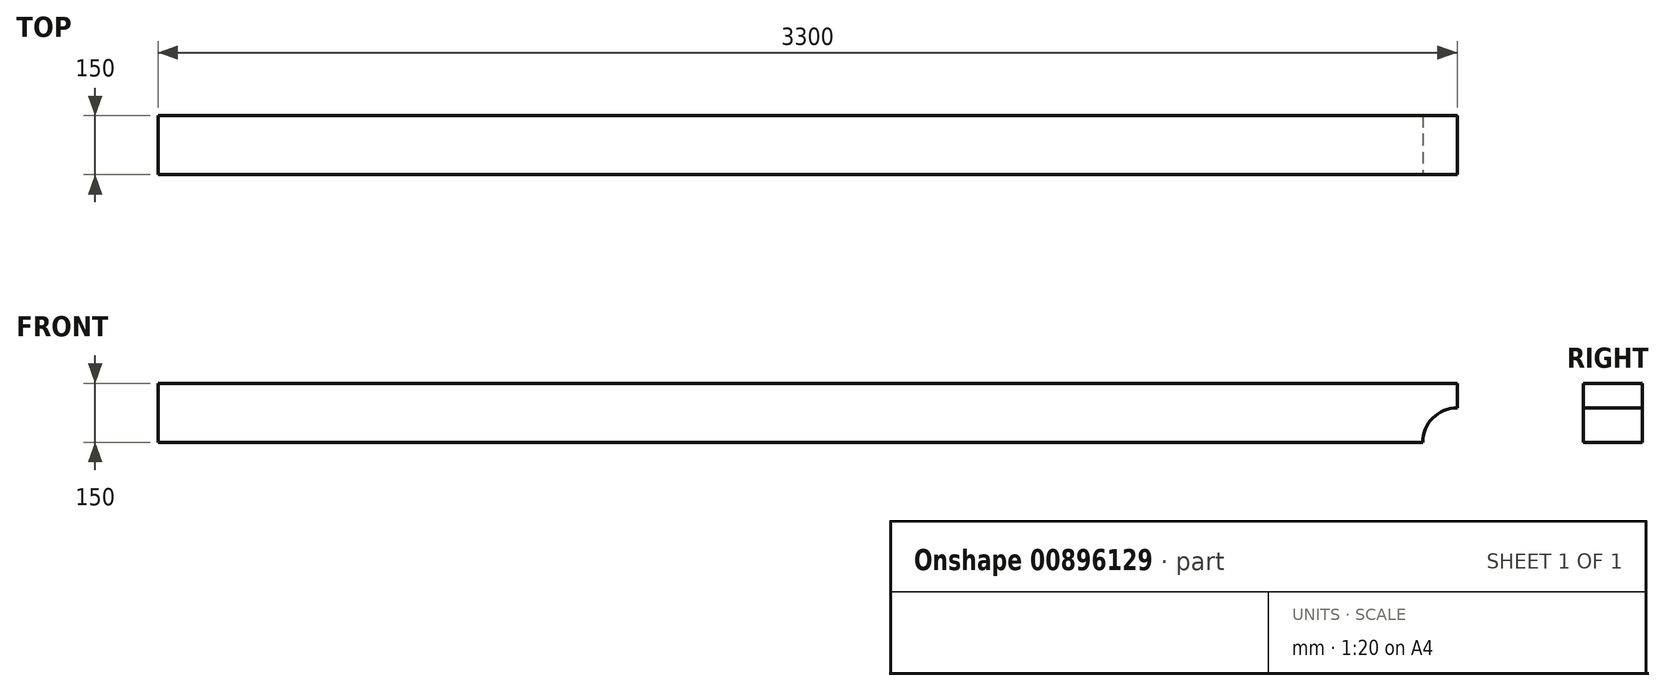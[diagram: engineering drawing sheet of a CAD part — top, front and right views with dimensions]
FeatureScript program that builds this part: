
annotation { "Feature Type Name" : "Feature", "Feature Type Description" : "" }
export const myFeature = defineFeature(function(context is Context, id is Id, definition is map)
    precondition{}
    {
        {
            var Q0;
            Q0=qCreatedBy(makeId("Front.planeOp"),FACE);
            var sketch = newSketch(context, id + "F0", { "sketchPlane" : qUnion([Q0])});
            skLineSegment(sketch, "E0.bottom", {"start": v(-3300, 150) * mm, "end": v(0, 150) * mm});
            skLineSegment(sketch, "E0.top", {"start": v(-3300, 0) * mm, "end": v(0, 0) * mm});
            skLineSegment(sketch, "E0.left", {"start": v(-3300, 150) * mm, "end": v(-3300, 0) * mm});
            skLineSegment(sketch, "E0.right", {"start": v(0, 150) * mm, "end": v(0, 0) * mm});
            skSolve(sketch);
        }
        {
            var Q0;
            Q0=makeQuery(id+"F0.imprint","IMPRINT",FACE,{"disambiguationData":[TD([[makeQuery(id+"F0.imprint","IMPRINT",EDGE,{"derivedFrom":sQuery(id+"F0.wireOp",EDGE,"E0.bottom")}),-1.0]])]});
            extrude(context, id + "F1", {"entities" : qUnion([Q0]), "oppositeDirection" : true, "depth" : 150 * mm, "offsetDistance" : 25 * mm});
        }
        {
            var Q0;
            Q0=sQuery(id+"F0.wireOp",VERTEX,"E0.top.end");
            var Q1;
            Q1=makeQuery(id+"F1.opExtrude","SWEPT_BODY",BODY,{"disambiguationData":[OSD([sQuery(id+"F0.wireOp",EDGE,"E0.bottom"),sQuery(id+"F0.wireOp",EDGE,"E0.top"),sQuery(id+"F0.wireOp",EDGE,"E0.left"),sQuery(id+"F0.wireOp",EDGE,"E0.right")])]});
            hole(context, id + "F2", {"style" : HoleStyle.SIMPLE, "endStyle" : HoleEndStyle.THROUGH, "holeDiameter" : 175 * mm, "majorDiameter" : 5 * mm, "isTappedThrough" : true, "tappedDepth" : 12 * mm, "tapClearance" : 3, "locations" : qUnion([Q0]), "scope" : qUnion([Q1])});
        }
    });
